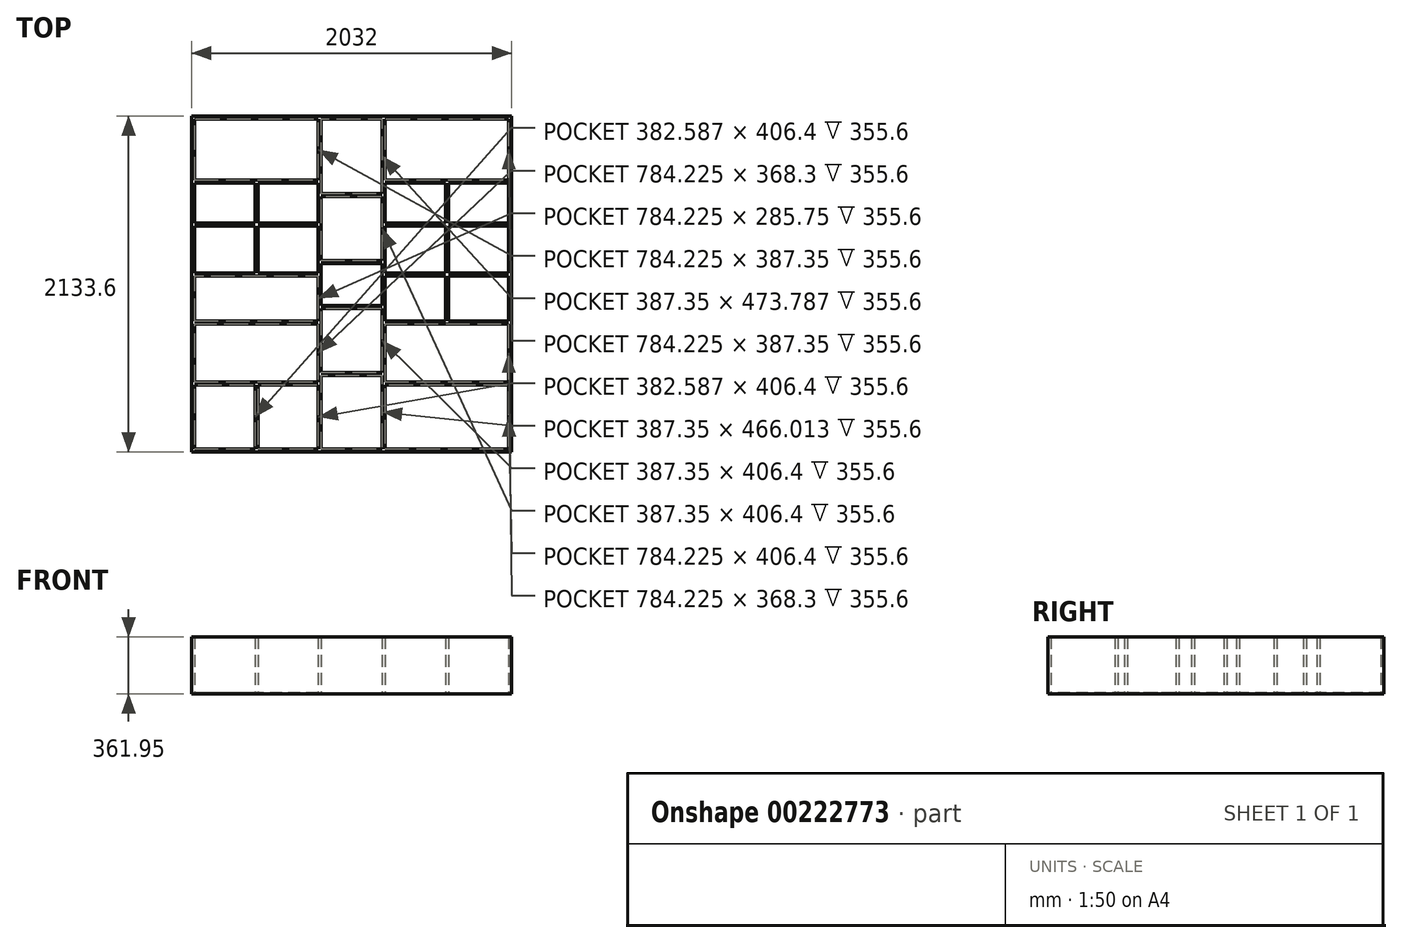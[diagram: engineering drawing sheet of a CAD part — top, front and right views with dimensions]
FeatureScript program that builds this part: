
annotation { "Feature Type Name" : "Feature", "Feature Type Description" : "" }
export const myFeature = defineFeature(function(context is Context, id is Id, definition is map)
    precondition{}
    {
        {
            var Q0;
            Q0=qCreatedBy(makeId("Top.planeOp"),FACE);
            var sketch = newSketch(context, id + "F0", { "sketchPlane" : qUnion([Q0])});
            skLineSegment(sketch, "E0.bottom", {"start": v(-1901.27, 1059.83) * mm, "end": v(130.73, 1059.83) * mm});
            skLineSegment(sketch, "E0.top", {"start": v(-1901.27, -1073.77) * mm, "end": v(130.73, -1073.77) * mm});
            skLineSegment(sketch, "E0.left", {"start": v(-1901.27, 1059.83) * mm, "end": v(-1901.27, -1073.77) * mm});
            skLineSegment(sketch, "E0.right", {"start": v(130.73, 1059.83) * mm, "end": v(130.73, -1073.77) * mm});
            skLineSegment(sketch, "E1", {"start": v(-1882.22, 1059.83) * mm, "end": v(-1882.22, -1073.77) * mm});
            skLineSegment(sketch, "E2", {"start": v(111.68, -1073.77) * mm, "end": v(111.68, 1059.83) * mm});
            skLineSegment(sketch, "E3", {"start": v(-682.07, 1059.83) * mm, "end": v(-682.07, 1132.47) * mm});
            skLineSegment(sketch, "E4", {"start": v(-1882.22, -1054.72) * mm, "end": v(111.68, -1054.72) * mm});
            skLineSegment(sketch, "E5", {"start": v(-1882.22, 1040.78) * mm, "end": v(111.68, 1040.78) * mm});
            skLineSegment(sketch, "E6", {"start": v(-672.55, 1040.78) * mm, "end": v(-672.55, -1054.72) * mm});
            skLineSegment(sketch, "E7", {"start": v(-691.6, 1040.78) * mm, "end": v(-691.6, -1054.72) * mm});
            skLineSegment(sketch, "E8.MirrorCS", {"start": v(-1078.95, 1040.78) * mm, "end": v(-1078.95, -1054.72) * mm});
            skLineSegment(sketch, "E9.MirrorCS", {"start": v(-1098, 1040.78) * mm, "end": v(-1098, -1054.72) * mm});
            skLineSegment(sketch, "E10", {"start": v(-672.55, 634.38) * mm, "end": v(111.68, 634.38) * mm});
            skLineSegment(sketch, "E11", {"start": v(-672.55, -648.32) * mm, "end": v(111.68, -648.32) * mm});
            skLineSegment(sketch, "E12", {"start": v(-672.55, -241.92) * mm, "end": v(111.68, -241.92) * mm});
            skLineSegment(sketch, "E13", {"start": v(-672.55, 62.88) * mm, "end": v(111.68, 62.88) * mm});
            skLineSegment(sketch, "E14", {"start": v(-672.55, 380.38) * mm, "end": v(111.68, 380.38) * mm});
            skLineSegment(sketch, "E15", {"start": v(-1078.95, -569.66) * mm, "end": v(-691.6, -569.66) * mm});
            skLineSegment(sketch, "E16", {"start": v(-1078.95, -163.26) * mm, "end": v(-691.6, -163.26) * mm});
            skLineSegment(sketch, "E17", {"start": v(-1078.95, 141.54) * mm, "end": v(-691.6, 141.54) * mm});
            skLineSegment(sketch, "E18", {"start": v(-1078.95, 547.94) * mm, "end": v(-691.6, 547.94) * mm});
            skLineSegment(sketch, "E19", {"start": v(-1098, -648.32) * mm, "end": v(-1882.22, -648.32) * mm});
            skLineSegment(sketch, "E20", {"start": v(-1098, -241.92) * mm, "end": v(-1882.22, -241.92) * mm});
            skLineSegment(sketch, "E21", {"start": v(-1098, 62.88) * mm, "end": v(-1882.22, 62.88) * mm});
            skLineSegment(sketch, "E22", {"start": v(-1098, 634.38) * mm, "end": v(-1882.22, 634.38) * mm});
            skLineSegment(sketch, "E23", {"start": v(-1882.22, 380.38) * mm, "end": v(-1098, 380.38) * mm});
            skLineSegment(sketch, "E24.0", {"start": v(-1098, 653.43) * mm, "end": v(-1882.22, 653.43) * mm});
            skLineSegment(sketch, "E25.0", {"start": v(-1098, -629.27) * mm, "end": v(-1882.22, -629.27) * mm});
            skLineSegment(sketch, "E26.0", {"start": v(-672.55, 653.43) * mm, "end": v(111.68, 653.43) * mm});
            skLineSegment(sketch, "E27.0", {"start": v(-672.55, -629.27) * mm, "end": v(111.68, -629.27) * mm});
            skLineSegment(sketch, "E28.0", {"start": v(-672.55, -260.97) * mm, "end": v(111.68, -260.97) * mm});
            skLineSegment(sketch, "E29.0", {"start": v(-1098, -260.97) * mm, "end": v(-1882.22, -260.97) * mm});
            skLineSegment(sketch, "E30.0", {"start": v(-1098, 43.83) * mm, "end": v(-1882.22, 43.83) * mm});
            skLineSegment(sketch, "E31.0", {"start": v(-672.55, 43.83) * mm, "end": v(111.68, 43.83) * mm});
            skLineSegment(sketch, "E32.0", {"start": v(-1882.22, 361.33) * mm, "end": v(-1098, 361.33) * mm});
            skLineSegment(sketch, "E33.0", {"start": v(-672.55, 361.33) * mm, "end": v(111.68, 361.33) * mm});
            skLineSegment(sketch, "E34.0", {"start": v(-1078.95, 567) * mm, "end": v(-691.6, 567) * mm});
            skLineSegment(sketch, "E35.0", {"start": v(-1078.95, -588.7) * mm, "end": v(-691.6, -588.7) * mm});
            skLineSegment(sketch, "E36.0", {"start": v(-1078.95, -144.2) * mm, "end": v(-691.6, -144.2) * mm});
            skLineSegment(sketch, "E37.0", {"start": v(-1078.95, 122.5) * mm, "end": v(-691.6, 122.5) * mm});
            skLineSegment(sketch, "E38.0", {"start": v(-1480.58, 62.88) * mm, "end": v(-1480.58, 634.38) * mm});
            skLineSegment(sketch, "E39.0", {"start": v(-1499.63, 62.88) * mm, "end": v(-1499.63, 634.38) * mm});
            skLineSegment(sketch, "E40.0", {"start": v(-289.96, -241.92) * mm, "end": v(-289.96, 634.38) * mm});
            skLineSegment(sketch, "E41.0", {"start": v(-270.9, -241.92) * mm, "end": v(-270.9, 634.38) * mm});
            skLineSegment(sketch, "E42.0", {"start": v(-1499.63, -648.32) * mm, "end": v(-1499.63, -1054.72) * mm});
            skLineSegment(sketch, "E43.0", {"start": v(-1480.58, -648.32) * mm, "end": v(-1480.58, -1054.72) * mm});
            skSolve(sketch);
        }
        {
            var Q0;
            {var subQ0=sQuery(id+"F0.wireOp",EDGE,"E12");var subQ1=sQuery(id+"F0.wireOp",EDGE,"E6");var subQ2=makeQuery(id+"F0.imprint","INTERSECT",VERTEX,{"derivedFrom":[subQ1,subQ0]});Q0=makeQuery(id+"F0.imprint","IMPRINT",FACE,{"disambiguationData":[TD([[makeQuery(id+"F0.imprint","IMPRINT",EDGE,{"disambiguationData":[TD([[subQ2,1.0]])],"derivedFrom":subQ1}),1.0]])]});}
            var Q1;
            {var subQ0=sQuery(id+"F0.wireOp",EDGE,"E15");Q1=makeQuery(id+"F0.imprint","IMPRINT",FACE,{"disambiguationData":[TD([[makeQuery(id+"F0.imprint","IMPRINT",EDGE,{"derivedFrom":subQ0}),1.0]])]});}
            var Q2;
            {var subQ0=sQuery(id+"F0.wireOp",EDGE,"E23");var subQ1=sQuery(id+"F0.wireOp",EDGE,"E9.MirrorCS");var subQ2=makeQuery(id+"F0.imprint","INTERSECT",VERTEX,{"derivedFrom":[subQ1,subQ0]});Q2=makeQuery(id+"F0.imprint","IMPRINT",FACE,{"disambiguationData":[TD([[makeQuery(id+"F0.imprint","IMPRINT",EDGE,{"disambiguationData":[TD([[subQ2,-1.0]])],"derivedFrom":subQ1}),-1.0]])]});}
            var Q3;
            {var subQ1=sQuery(id+"F0.wireOp",EDGE,"E1");var subQ5=sQuery(id+"F0.wireOp",EDGE,"E0.top");var subQ10=makeQuery(id+"F0.imprint","INTERSECT",VERTEX,{"derivedFrom":[subQ5,subQ1]});Q3=makeQuery(id+"F0.imprint","IMPRINT",FACE,{"disambiguationData":[TD([[makeQuery(id+"F0.imprint","IMPRINT",EDGE,{"disambiguationData":[TD([[subQ10,-1.0]])],"derivedFrom":subQ5}),1.0]])]});}
            var Q4;
            {var subQ0=sQuery(id+"F0.wireOp",EDGE,"E14");var subQ1=sQuery(id+"F0.wireOp",EDGE,"E2");var subQ2=makeQuery(id+"F0.imprint","INTERSECT",VERTEX,{"derivedFrom":[subQ1,subQ0]});Q4=makeQuery(id+"F0.imprint","IMPRINT",FACE,{"disambiguationData":[TD([[makeQuery(id+"F0.imprint","IMPRINT",EDGE,{"disambiguationData":[TD([[subQ2,1.0]])],"derivedFrom":subQ1}),1.0]])]});}
            var Q5;
            {var subQ0=sQuery(id+"F0.wireOp",EDGE,"E13");var subQ1=sQuery(id+"F0.wireOp",EDGE,"E2");var subQ2=makeQuery(id+"F0.imprint","INTERSECT",VERTEX,{"derivedFrom":[subQ1,subQ0]});Q5=makeQuery(id+"F0.imprint","IMPRINT",FACE,{"disambiguationData":[TD([[makeQuery(id+"F0.imprint","IMPRINT",EDGE,{"disambiguationData":[TD([[subQ2,-1.0]])],"derivedFrom":subQ1}),1.0]])]});}
            var Q6;
            {var subQ0=sQuery(id+"F0.wireOp",EDGE,"E10");var subQ1=sQuery(id+"F0.wireOp",EDGE,"E2");var subQ2=makeQuery(id+"F0.imprint","INTERSECT",VERTEX,{"derivedFrom":[subQ1,subQ0]});Q6=makeQuery(id+"F0.imprint","IMPRINT",FACE,{"disambiguationData":[TD([[makeQuery(id+"F0.imprint","IMPRINT",EDGE,{"disambiguationData":[TD([[subQ2,1.0]])],"derivedFrom":subQ1}),1.0]])]});}
            var Q7;
            {var subQ3=sQuery(id+"F0.wireOp",EDGE,"E43.0");Q7=makeQuery(id+"F0.imprint","IMPRINT",FACE,{"disambiguationData":[TD([[makeQuery(id+"F0.imprint","IMPRINT",EDGE,{"derivedFrom":subQ3}),1.0]])]});}
            var Q8;
            {var subQ0=sQuery(id+"F0.wireOp",EDGE,"E13");var subQ1=sQuery(id+"F0.wireOp",EDGE,"E6");var subQ2=makeQuery(id+"F0.imprint","INTERSECT",VERTEX,{"derivedFrom":[subQ1,subQ0]});Q8=makeQuery(id+"F0.imprint","IMPRINT",FACE,{"disambiguationData":[TD([[makeQuery(id+"F0.imprint","IMPRINT",EDGE,{"disambiguationData":[TD([[subQ2,-1.0]])],"derivedFrom":subQ1}),1.0]])]});}
            var Q9;
            {var subQ0=sQuery(id+"F0.wireOp",EDGE,"E14");var subQ1=sQuery(id+"F0.wireOp",EDGE,"E6");var subQ2=makeQuery(id+"F0.imprint","INTERSECT",VERTEX,{"derivedFrom":[subQ1,subQ0]});Q9=makeQuery(id+"F0.imprint","IMPRINT",FACE,{"disambiguationData":[TD([[makeQuery(id+"F0.imprint","IMPRINT",EDGE,{"disambiguationData":[TD([[subQ2,-1.0]])],"derivedFrom":subQ1}),1.0]])]});}
            var Q10;
            {var subQ0=sQuery(id+"F0.wireOp",EDGE,"E6");var subQ16=sQuery(id+"F0.wireOp",EDGE,"E4");var subQ17=makeQuery(id+"F0.imprint","INTERSECT",VERTEX,{"derivedFrom":[subQ16,subQ0]});Q10=makeQuery(id+"F0.imprint","IMPRINT",FACE,{"disambiguationData":[TD([[makeQuery(id+"F0.imprint","IMPRINT",EDGE,{"disambiguationData":[TD([[subQ17,1.0]])],"derivedFrom":subQ16}),1.0]])]});}
            var Q11;
            {var subQ0=sQuery(id+"F0.wireOp",EDGE,"E17");Q11=makeQuery(id+"F0.imprint","IMPRINT",FACE,{"disambiguationData":[TD([[makeQuery(id+"F0.imprint","IMPRINT",EDGE,{"derivedFrom":subQ0}),-1.0]])]});}
            var Q12;
            {var subQ7=sQuery(id+"F0.wireOp",EDGE,"E24.0");Q12=makeQuery(id+"F0.imprint","IMPRINT",FACE,{"disambiguationData":[TD([[makeQuery(id+"F0.imprint","IMPRINT",EDGE,{"derivedFrom":subQ7}),1.0]])]});}
            var Q13;
            {var subQ0=sQuery(id+"F0.wireOp",EDGE,"E16");Q13=makeQuery(id+"F0.imprint","IMPRINT",FACE,{"disambiguationData":[TD([[makeQuery(id+"F0.imprint","IMPRINT",EDGE,{"derivedFrom":subQ0}),1.0]])]});}
            var Q14;
            {var subQ1=sQuery(id+"F0.wireOp",EDGE,"E0.bottom");var subQ8=makeQuery(id+"F0.imprint","IMPRINT",VERTEX,{"derivedFrom":subQ1});Q14=makeQuery(id+"F0.imprint","IMPRINT",FACE,{"disambiguationData":[TD([[makeQuery(id+"F0.imprint","IMPRINT",EDGE,{"disambiguationData":[TD([[subQ8,1.0]])],"derivedFrom":subQ1}),-1.0]])]});}
            var Q15;
            {var subQ0=sQuery(id+"F0.wireOp",EDGE,"E22");var subQ1=sQuery(id+"F0.wireOp",EDGE,"E9.MirrorCS");var subQ2=makeQuery(id+"F0.imprint","INTERSECT",VERTEX,{"derivedFrom":[subQ1,subQ0]});Q15=makeQuery(id+"F0.imprint","IMPRINT",FACE,{"disambiguationData":[TD([[makeQuery(id+"F0.imprint","IMPRINT",EDGE,{"disambiguationData":[TD([[subQ2,-1.0]])],"derivedFrom":subQ1}),-1.0]])]});}
            var Q16;
            {var subQ5=sQuery(id+"F0.wireOp",EDGE,"E25.0");Q16=makeQuery(id+"F0.imprint","IMPRINT",FACE,{"disambiguationData":[TD([[makeQuery(id+"F0.imprint","IMPRINT",EDGE,{"derivedFrom":subQ5}),1.0]])]});}
            var Q17;
            {var subQ0=sQuery(id+"F0.wireOp",EDGE,"E8.MirrorCS");var subQ15=sQuery(id+"F0.wireOp",EDGE,"E4");var subQ16=makeQuery(id+"F0.imprint","INTERSECT",VERTEX,{"derivedFrom":[subQ15,subQ0]});Q17=makeQuery(id+"F0.imprint","IMPRINT",FACE,{"disambiguationData":[TD([[makeQuery(id+"F0.imprint","IMPRINT",EDGE,{"disambiguationData":[TD([[subQ16,1.0]])],"derivedFrom":subQ15}),1.0]])]});}
            var Q18;
            {var subQ0=sQuery(id+"F0.wireOp",EDGE,"E42.0");Q18=makeQuery(id+"F0.imprint","IMPRINT",FACE,{"disambiguationData":[TD([[makeQuery(id+"F0.imprint","IMPRINT",EDGE,{"derivedFrom":subQ0}),1.0]])]});}
            var Q19;
            {var subQ0=sQuery(id+"F0.wireOp",EDGE,"E40.0");var subQ1=sQuery(id+"F0.wireOp",EDGE,"E13");var subQ2=makeQuery(id+"F0.imprint","INTERSECT",VERTEX,{"derivedFrom":[subQ1,subQ0]});Q19=makeQuery(id+"F0.imprint","IMPRINT",FACE,{"disambiguationData":[TD([[makeQuery(id+"F0.imprint","IMPRINT",EDGE,{"disambiguationData":[TD([[subQ2,-1.0]])],"derivedFrom":subQ1}),1.0]])]});}
            var Q20;
            {var subQ0=sQuery(id+"F0.wireOp",EDGE,"E13");var subQ1=sQuery(id+"F0.wireOp",EDGE,"E6");var subQ2=makeQuery(id+"F0.imprint","INTERSECT",VERTEX,{"derivedFrom":[subQ1,subQ0]});Q20=makeQuery(id+"F0.imprint","IMPRINT",FACE,{"disambiguationData":[TD([[makeQuery(id+"F0.imprint","IMPRINT",EDGE,{"disambiguationData":[TD([[subQ2,1.0]])],"derivedFrom":subQ1}),1.0]])]});}
            var Q21;
            {var subQ0=sQuery(id+"F0.wireOp",EDGE,"E10");var subQ1=sQuery(id+"F0.wireOp",EDGE,"E6");var subQ2=makeQuery(id+"F0.imprint","INTERSECT",VERTEX,{"derivedFrom":[subQ1,subQ0]});Q21=makeQuery(id+"F0.imprint","IMPRINT",FACE,{"disambiguationData":[TD([[makeQuery(id+"F0.imprint","IMPRINT",EDGE,{"disambiguationData":[TD([[subQ2,-1.0]])],"derivedFrom":subQ1}),1.0]])]});}
            var Q22;
            {var subQ0=sQuery(id+"F0.wireOp",EDGE,"E13");var subQ1=sQuery(id+"F0.wireOp",EDGE,"E2");var subQ2=makeQuery(id+"F0.imprint","INTERSECT",VERTEX,{"derivedFrom":[subQ1,subQ0]});Q22=makeQuery(id+"F0.imprint","IMPRINT",FACE,{"disambiguationData":[TD([[makeQuery(id+"F0.imprint","IMPRINT",EDGE,{"disambiguationData":[TD([[subQ2,1.0]])],"derivedFrom":subQ1}),1.0]])]});}
            var Q23;
            {var subQ0=sQuery(id+"F0.wireOp",EDGE,"E21");var subQ1=sQuery(id+"F0.wireOp",EDGE,"E9.MirrorCS");var subQ2=makeQuery(id+"F0.imprint","INTERSECT",VERTEX,{"derivedFrom":[subQ1,subQ0]});Q23=makeQuery(id+"F0.imprint","IMPRINT",FACE,{"disambiguationData":[TD([[makeQuery(id+"F0.imprint","IMPRINT",EDGE,{"disambiguationData":[TD([[subQ2,1.0]])],"derivedFrom":subQ1}),-1.0]])]});}
            var Q24;
            {var subQ0=sQuery(id+"F0.wireOp",EDGE,"E12");var subQ1=sQuery(id+"F0.wireOp",EDGE,"E2");var subQ2=makeQuery(id+"F0.imprint","INTERSECT",VERTEX,{"derivedFrom":[subQ1,subQ0]});Q24=makeQuery(id+"F0.imprint","IMPRINT",FACE,{"disambiguationData":[TD([[makeQuery(id+"F0.imprint","IMPRINT",EDGE,{"disambiguationData":[TD([[subQ2,-1.0]])],"derivedFrom":subQ1}),1.0]])]});}
            var Q25;
            {var subQ3=sQuery(id+"F0.wireOp",EDGE,"E11");Q25=makeQuery(id+"F0.imprint","IMPRINT",FACE,{"disambiguationData":[TD([[makeQuery(id+"F0.imprint","IMPRINT",EDGE,{"derivedFrom":subQ3}),-1.0]])]});}
            var Q26;
            {var subQ0=sQuery(id+"F0.wireOp",EDGE,"E11");Q26=makeQuery(id+"F0.imprint","IMPRINT",FACE,{"disambiguationData":[TD([[makeQuery(id+"F0.imprint","IMPRINT",EDGE,{"derivedFrom":subQ0}),1.0]])]});}
            var Q27;
            {var subQ0=sQuery(id+"F0.wireOp",EDGE,"E27.0");Q27=makeQuery(id+"F0.imprint","IMPRINT",FACE,{"disambiguationData":[TD([[makeQuery(id+"F0.imprint","IMPRINT",EDGE,{"derivedFrom":subQ0}),1.0]])]});}
            var Q28;
            {var subQ5=sQuery(id+"F0.wireOp",EDGE,"E42.0");Q28=makeQuery(id+"F0.imprint","IMPRINT",FACE,{"disambiguationData":[TD([[makeQuery(id+"F0.imprint","IMPRINT",EDGE,{"derivedFrom":subQ5}),-1.0]])]});}
            var Q29;
            {var subQ0=sQuery(id+"F0.wireOp",EDGE,"E25.0");Q29=makeQuery(id+"F0.imprint","IMPRINT",FACE,{"disambiguationData":[TD([[makeQuery(id+"F0.imprint","IMPRINT",EDGE,{"derivedFrom":subQ0}),-1.0]])]});}
            var Q30;
            {var subQ0=sQuery(id+"F0.wireOp",EDGE,"E17");Q30=makeQuery(id+"F0.imprint","IMPRINT",FACE,{"disambiguationData":[TD([[makeQuery(id+"F0.imprint","IMPRINT",EDGE,{"derivedFrom":subQ0}),1.0]])]});}
            var Q31;
            {var subQ0=sQuery(id+"F0.wireOp",EDGE,"E20");Q31=makeQuery(id+"F0.imprint","IMPRINT",FACE,{"disambiguationData":[TD([[makeQuery(id+"F0.imprint","IMPRINT",EDGE,{"derivedFrom":subQ0}),1.0]])]});}
            var Q32;
            {var subQ0=sQuery(id+"F0.wireOp",EDGE,"E20");Q32=makeQuery(id+"F0.imprint","IMPRINT",FACE,{"disambiguationData":[TD([[makeQuery(id+"F0.imprint","IMPRINT",EDGE,{"derivedFrom":subQ0}),-1.0]])]});}
            var Q33;
            {var subQ0=sQuery(id+"F0.wireOp",EDGE,"E21");var subQ1=sQuery(id+"F0.wireOp",EDGE,"E1");var subQ2=makeQuery(id+"F0.imprint","INTERSECT",VERTEX,{"derivedFrom":[subQ1,subQ0]});Q33=makeQuery(id+"F0.imprint","IMPRINT",FACE,{"disambiguationData":[TD([[makeQuery(id+"F0.imprint","IMPRINT",EDGE,{"disambiguationData":[TD([[subQ2,1.0]])],"derivedFrom":subQ1}),1.0]])]});}
            var Q34;
            {var subQ0=sQuery(id+"F0.wireOp",EDGE,"E23");var subQ1=sQuery(id+"F0.wireOp",EDGE,"E1");var subQ2=makeQuery(id+"F0.imprint","INTERSECT",VERTEX,{"derivedFrom":[subQ1,subQ0]});Q34=makeQuery(id+"F0.imprint","IMPRINT",FACE,{"disambiguationData":[TD([[makeQuery(id+"F0.imprint","IMPRINT",EDGE,{"disambiguationData":[TD([[subQ2,-1.0]])],"derivedFrom":subQ1}),1.0]])]});}
            var Q35;
            {var subQ0=sQuery(id+"F0.wireOp",EDGE,"E22");var subQ1=sQuery(id+"F0.wireOp",EDGE,"E1");var subQ2=makeQuery(id+"F0.imprint","INTERSECT",VERTEX,{"derivedFrom":[subQ1,subQ0]});Q35=makeQuery(id+"F0.imprint","IMPRINT",FACE,{"disambiguationData":[TD([[makeQuery(id+"F0.imprint","IMPRINT",EDGE,{"disambiguationData":[TD([[subQ2,-1.0]])],"derivedFrom":subQ1}),1.0]])]});}
            var Q36;
            {var subQ13=sQuery(id+"F0.wireOp",EDGE,"E0.left");Q36=makeQuery(id+"F0.imprint","IMPRINT",FACE,{"disambiguationData":[TD([[makeQuery(id+"F0.imprint","IMPRINT",EDGE,{"derivedFrom":subQ13}),1.0]])]});}
            var Q37;
            {var subQ0=sQuery(id+"F0.wireOp",EDGE,"E36.0");Q37=makeQuery(id+"F0.imprint","IMPRINT",FACE,{"disambiguationData":[TD([[makeQuery(id+"F0.imprint","IMPRINT",EDGE,{"derivedFrom":subQ0}),1.0]])]});}
            var Q38;
            {var subQ5=sQuery(id+"F0.wireOp",EDGE,"E30.0");Q38=makeQuery(id+"F0.imprint","IMPRINT",FACE,{"disambiguationData":[TD([[makeQuery(id+"F0.imprint","IMPRINT",EDGE,{"derivedFrom":subQ5}),-1.0]])]});}
            var Q39;
            {var subQ13=sQuery(id+"F0.wireOp",EDGE,"E0.right");Q39=makeQuery(id+"F0.imprint","IMPRINT",FACE,{"disambiguationData":[TD([[makeQuery(id+"F0.imprint","IMPRINT",EDGE,{"derivedFrom":subQ13}),-1.0]])]});}
            var Q40;
            {var subQ3=sQuery(id+"F0.wireOp",EDGE,"E24.0");Q40=makeQuery(id+"F0.imprint","IMPRINT",FACE,{"disambiguationData":[TD([[makeQuery(id+"F0.imprint","IMPRINT",EDGE,{"derivedFrom":subQ3}),-1.0]])]});}
            var Q41;
            {var subQ0=sQuery(id+"F0.wireOp",EDGE,"E15");Q41=makeQuery(id+"F0.imprint","IMPRINT",FACE,{"disambiguationData":[TD([[makeQuery(id+"F0.imprint","IMPRINT",EDGE,{"derivedFrom":subQ0}),-1.0]])]});}
            var Q42;
            {var subQ5=sQuery(id+"F0.wireOp",EDGE,"E26.0");Q42=makeQuery(id+"F0.imprint","IMPRINT",FACE,{"disambiguationData":[TD([[makeQuery(id+"F0.imprint","IMPRINT",EDGE,{"derivedFrom":subQ5}),-1.0]])]});}
            var Q43;
            {var subQ5=sQuery(id+"F0.wireOp",EDGE,"E34.0");Q43=makeQuery(id+"F0.imprint","IMPRINT",FACE,{"disambiguationData":[TD([[makeQuery(id+"F0.imprint","IMPRINT",EDGE,{"derivedFrom":subQ5}),1.0]])]});}
            var Q44;
            {var subQ5=sQuery(id+"F0.wireOp",EDGE,"E35.0");Q44=makeQuery(id+"F0.imprint","IMPRINT",FACE,{"disambiguationData":[TD([[makeQuery(id+"F0.imprint","IMPRINT",EDGE,{"derivedFrom":subQ5}),-1.0]])]});}
            var Q45;
            {var subQ3=sQuery(id+"F0.wireOp",EDGE,"E26.0");Q45=makeQuery(id+"F0.imprint","IMPRINT",FACE,{"disambiguationData":[TD([[makeQuery(id+"F0.imprint","IMPRINT",EDGE,{"derivedFrom":subQ3}),1.0]])]});}
            var Q46;
            {var subQ0=sQuery(id+"F0.wireOp",EDGE,"E18");Q46=makeQuery(id+"F0.imprint","IMPRINT",FACE,{"disambiguationData":[TD([[makeQuery(id+"F0.imprint","IMPRINT",EDGE,{"derivedFrom":subQ0}),1.0]])]});}
            var Q47;
            {var subQ5=sQuery(id+"F0.wireOp",EDGE,"E28.0");Q47=makeQuery(id+"F0.imprint","IMPRINT",FACE,{"disambiguationData":[TD([[makeQuery(id+"F0.imprint","IMPRINT",EDGE,{"derivedFrom":subQ5}),1.0]])]});}
            var Q48;
            {var subQ0=sQuery(id+"F0.wireOp",EDGE,"E38.0");var subQ1=sQuery(id+"F0.wireOp",EDGE,"E21");var subQ2=makeQuery(id+"F0.imprint","INTERSECT",VERTEX,{"derivedFrom":[subQ1,subQ0]});Q48=makeQuery(id+"F0.imprint","IMPRINT",FACE,{"disambiguationData":[TD([[makeQuery(id+"F0.imprint","IMPRINT",EDGE,{"disambiguationData":[TD([[subQ2,-1.0]])],"derivedFrom":subQ1}),-1.0]])]});}
            var Q49;
            {var subQ0=sQuery(id+"F0.wireOp",EDGE,"E40.0");var subQ1=sQuery(id+"F0.wireOp",EDGE,"E14");var subQ2=makeQuery(id+"F0.imprint","INTERSECT",VERTEX,{"derivedFrom":[subQ1,subQ0]});Q49=makeQuery(id+"F0.imprint","IMPRINT",FACE,{"disambiguationData":[TD([[makeQuery(id+"F0.imprint","IMPRINT",EDGE,{"disambiguationData":[TD([[subQ2,-1.0]])],"derivedFrom":subQ1}),-1.0]])]});}
            var Q50;
            {var subQ0=sQuery(id+"F0.wireOp",EDGE,"E40.0");var subQ1=sQuery(id+"F0.wireOp",EDGE,"E13");var subQ2=makeQuery(id+"F0.imprint","INTERSECT",VERTEX,{"derivedFrom":[subQ1,subQ0]});Q50=makeQuery(id+"F0.imprint","IMPRINT",FACE,{"disambiguationData":[TD([[makeQuery(id+"F0.imprint","IMPRINT",EDGE,{"disambiguationData":[TD([[subQ2,-1.0]])],"derivedFrom":subQ1}),-1.0]])]});}
            var Q51;
            {var subQ0=sQuery(id+"F0.wireOp",EDGE,"E40.0");var subQ1=sQuery(id+"F0.wireOp",EDGE,"E12");var subQ2=makeQuery(id+"F0.imprint","INTERSECT",VERTEX,{"derivedFrom":[subQ1,subQ0]});Q51=makeQuery(id+"F0.imprint","IMPRINT",FACE,{"disambiguationData":[TD([[makeQuery(id+"F0.imprint","IMPRINT",EDGE,{"disambiguationData":[TD([[subQ2,-1.0]])],"derivedFrom":subQ1}),1.0]])]});}
            var Q52;
            {var subQ0=sQuery(id+"F0.wireOp",EDGE,"E39.0");var subQ1=sQuery(id+"F0.wireOp",EDGE,"E23");var subQ2=makeQuery(id+"F0.imprint","INTERSECT",VERTEX,{"derivedFrom":[subQ1,subQ0]});Q52=makeQuery(id+"F0.imprint","IMPRINT",FACE,{"disambiguationData":[TD([[makeQuery(id+"F0.imprint","IMPRINT",EDGE,{"disambiguationData":[TD([[subQ2,-1.0]])],"derivedFrom":subQ1}),-1.0]])]});}
            var Q53;
            {var subQ0=sQuery(id+"F0.wireOp",EDGE,"E40.0");var subQ1=sQuery(id+"F0.wireOp",EDGE,"E10");var subQ2=makeQuery(id+"F0.imprint","INTERSECT",VERTEX,{"derivedFrom":[subQ1,subQ0]});Q53=makeQuery(id+"F0.imprint","IMPRINT",FACE,{"disambiguationData":[TD([[makeQuery(id+"F0.imprint","IMPRINT",EDGE,{"disambiguationData":[TD([[subQ2,-1.0]])],"derivedFrom":subQ1}),-1.0]])]});}
            var Q54;
            {var subQ0=sQuery(id+"F0.wireOp",EDGE,"E38.0");var subQ1=sQuery(id+"F0.wireOp",EDGE,"E22");var subQ2=makeQuery(id+"F0.imprint","INTERSECT",VERTEX,{"derivedFrom":[subQ1,subQ0]});Q54=makeQuery(id+"F0.imprint","IMPRINT",FACE,{"disambiguationData":[TD([[makeQuery(id+"F0.imprint","IMPRINT",EDGE,{"disambiguationData":[TD([[subQ2,-1.0]])],"derivedFrom":subQ1}),1.0]])]});}
            extrude(context, id + "F1", {"entities" : qUnion([Q0, Q1, Q2, Q3, Q4, Q5, Q6, Q7, Q8, Q9, Q10, Q11, Q12, Q13, Q14, Q15, Q16, Q17, Q18, Q19, Q20, Q21, Q22, Q23, Q24, Q25, Q26, Q27, Q28, Q29, Q30, Q31, Q32, Q33, Q34, Q35, Q36, Q37, Q38, Q39, Q40, Q41, Q42, Q43, Q44, Q45, Q46, Q47, Q48, Q49, Q50, Q51, Q52, Q53, Q54]), "oppositeDirection" : true, "depth" : 6.35 * mm});
        }
        {
            var Q0;
            {var subQ13=sQuery(id+"F0.wireOp",EDGE,"E0.left");Q0=makeQuery(id+"F0.imprint","IMPRINT",FACE,{"disambiguationData":[TD([[makeQuery(id+"F0.imprint","IMPRINT",EDGE,{"derivedFrom":subQ13}),1.0]])]});}
            var Q1;
            {var subQ1=sQuery(id+"F0.wireOp",EDGE,"E0.bottom");var subQ8=makeQuery(id+"F0.imprint","IMPRINT",VERTEX,{"derivedFrom":subQ1});Q1=makeQuery(id+"F0.imprint","IMPRINT",FACE,{"disambiguationData":[TD([[makeQuery(id+"F0.imprint","IMPRINT",EDGE,{"disambiguationData":[TD([[subQ8,1.0]])],"derivedFrom":subQ1}),-1.0]])]});}
            var Q2;
            {var subQ7=sQuery(id+"F0.wireOp",EDGE,"E24.0");Q2=makeQuery(id+"F0.imprint","IMPRINT",FACE,{"disambiguationData":[TD([[makeQuery(id+"F0.imprint","IMPRINT",EDGE,{"derivedFrom":subQ7}),1.0]])]});}
            var Q3;
            {var subQ0=sQuery(id+"F0.wireOp",EDGE,"E38.0");var subQ1=sQuery(id+"F0.wireOp",EDGE,"E22");var subQ2=makeQuery(id+"F0.imprint","INTERSECT",VERTEX,{"derivedFrom":[subQ1,subQ0]});Q3=makeQuery(id+"F0.imprint","IMPRINT",FACE,{"disambiguationData":[TD([[makeQuery(id+"F0.imprint","IMPRINT",EDGE,{"disambiguationData":[TD([[subQ2,-1.0]])],"derivedFrom":subQ1}),1.0]])]});}
            var Q4;
            {var subQ0=sQuery(id+"F0.wireOp",EDGE,"E23");var subQ1=sQuery(id+"F0.wireOp",EDGE,"E1");var subQ2=makeQuery(id+"F0.imprint","INTERSECT",VERTEX,{"derivedFrom":[subQ1,subQ0]});Q4=makeQuery(id+"F0.imprint","IMPRINT",FACE,{"disambiguationData":[TD([[makeQuery(id+"F0.imprint","IMPRINT",EDGE,{"disambiguationData":[TD([[subQ2,-1.0]])],"derivedFrom":subQ1}),1.0]])]});}
            var Q5;
            {var subQ0=sQuery(id+"F0.wireOp",EDGE,"E39.0");var subQ1=sQuery(id+"F0.wireOp",EDGE,"E23");var subQ2=makeQuery(id+"F0.imprint","INTERSECT",VERTEX,{"derivedFrom":[subQ1,subQ0]});Q5=makeQuery(id+"F0.imprint","IMPRINT",FACE,{"disambiguationData":[TD([[makeQuery(id+"F0.imprint","IMPRINT",EDGE,{"disambiguationData":[TD([[subQ2,-1.0]])],"derivedFrom":subQ1}),-1.0]])]});}
            var Q6;
            {var subQ0=sQuery(id+"F0.wireOp",EDGE,"E23");var subQ1=sQuery(id+"F0.wireOp",EDGE,"E9.MirrorCS");var subQ2=makeQuery(id+"F0.imprint","INTERSECT",VERTEX,{"derivedFrom":[subQ1,subQ0]});Q6=makeQuery(id+"F0.imprint","IMPRINT",FACE,{"disambiguationData":[TD([[makeQuery(id+"F0.imprint","IMPRINT",EDGE,{"disambiguationData":[TD([[subQ2,-1.0]])],"derivedFrom":subQ1}),-1.0]])]});}
            var Q7;
            {var subQ0=sQuery(id+"F0.wireOp",EDGE,"E38.0");var subQ1=sQuery(id+"F0.wireOp",EDGE,"E21");var subQ2=makeQuery(id+"F0.imprint","INTERSECT",VERTEX,{"derivedFrom":[subQ1,subQ0]});Q7=makeQuery(id+"F0.imprint","IMPRINT",FACE,{"disambiguationData":[TD([[makeQuery(id+"F0.imprint","IMPRINT",EDGE,{"disambiguationData":[TD([[subQ2,-1.0]])],"derivedFrom":subQ1}),-1.0]])]});}
            var Q8;
            {var subQ5=sQuery(id+"F0.wireOp",EDGE,"E30.0");Q8=makeQuery(id+"F0.imprint","IMPRINT",FACE,{"disambiguationData":[TD([[makeQuery(id+"F0.imprint","IMPRINT",EDGE,{"derivedFrom":subQ5}),-1.0]])]});}
            var Q9;
            {var subQ0=sQuery(id+"F0.wireOp",EDGE,"E20");Q9=makeQuery(id+"F0.imprint","IMPRINT",FACE,{"disambiguationData":[TD([[makeQuery(id+"F0.imprint","IMPRINT",EDGE,{"derivedFrom":subQ0}),1.0]])]});}
            var Q10;
            {var subQ5=sQuery(id+"F0.wireOp",EDGE,"E25.0");Q10=makeQuery(id+"F0.imprint","IMPRINT",FACE,{"disambiguationData":[TD([[makeQuery(id+"F0.imprint","IMPRINT",EDGE,{"derivedFrom":subQ5}),1.0]])]});}
            var Q11;
            {var subQ0=sQuery(id+"F0.wireOp",EDGE,"E42.0");Q11=makeQuery(id+"F0.imprint","IMPRINT",FACE,{"disambiguationData":[TD([[makeQuery(id+"F0.imprint","IMPRINT",EDGE,{"derivedFrom":subQ0}),1.0]])]});}
            var Q12;
            {var subQ0=sQuery(id+"F0.wireOp",EDGE,"E8.MirrorCS");var subQ15=sQuery(id+"F0.wireOp",EDGE,"E4");var subQ16=makeQuery(id+"F0.imprint","INTERSECT",VERTEX,{"derivedFrom":[subQ15,subQ0]});Q12=makeQuery(id+"F0.imprint","IMPRINT",FACE,{"disambiguationData":[TD([[makeQuery(id+"F0.imprint","IMPRINT",EDGE,{"disambiguationData":[TD([[subQ16,1.0]])],"derivedFrom":subQ15}),1.0]])]});}
            var Q13;
            {var subQ1=sQuery(id+"F0.wireOp",EDGE,"E1");var subQ5=sQuery(id+"F0.wireOp",EDGE,"E0.top");var subQ10=makeQuery(id+"F0.imprint","INTERSECT",VERTEX,{"derivedFrom":[subQ5,subQ1]});Q13=makeQuery(id+"F0.imprint","IMPRINT",FACE,{"disambiguationData":[TD([[makeQuery(id+"F0.imprint","IMPRINT",EDGE,{"disambiguationData":[TD([[subQ10,-1.0]])],"derivedFrom":subQ5}),1.0]])]});}
            var Q14;
            {var subQ0=sQuery(id+"F0.wireOp",EDGE,"E18");Q14=makeQuery(id+"F0.imprint","IMPRINT",FACE,{"disambiguationData":[TD([[makeQuery(id+"F0.imprint","IMPRINT",EDGE,{"derivedFrom":subQ0}),1.0]])]});}
            var Q15;
            {var subQ0=sQuery(id+"F0.wireOp",EDGE,"E17");Q15=makeQuery(id+"F0.imprint","IMPRINT",FACE,{"disambiguationData":[TD([[makeQuery(id+"F0.imprint","IMPRINT",EDGE,{"derivedFrom":subQ0}),-1.0]])]});}
            var Q16;
            {var subQ0=sQuery(id+"F0.wireOp",EDGE,"E16");Q16=makeQuery(id+"F0.imprint","IMPRINT",FACE,{"disambiguationData":[TD([[makeQuery(id+"F0.imprint","IMPRINT",EDGE,{"derivedFrom":subQ0}),1.0]])]});}
            var Q17;
            {var subQ0=sQuery(id+"F0.wireOp",EDGE,"E15");Q17=makeQuery(id+"F0.imprint","IMPRINT",FACE,{"disambiguationData":[TD([[makeQuery(id+"F0.imprint","IMPRINT",EDGE,{"derivedFrom":subQ0}),-1.0]])]});}
            var Q18;
            {var subQ0=sQuery(id+"F0.wireOp",EDGE,"E6");var subQ16=sQuery(id+"F0.wireOp",EDGE,"E4");var subQ17=makeQuery(id+"F0.imprint","INTERSECT",VERTEX,{"derivedFrom":[subQ16,subQ0]});Q18=makeQuery(id+"F0.imprint","IMPRINT",FACE,{"disambiguationData":[TD([[makeQuery(id+"F0.imprint","IMPRINT",EDGE,{"disambiguationData":[TD([[subQ17,1.0]])],"derivedFrom":subQ16}),1.0]])]});}
            var Q19;
            {var subQ5=sQuery(id+"F0.wireOp",EDGE,"E26.0");Q19=makeQuery(id+"F0.imprint","IMPRINT",FACE,{"disambiguationData":[TD([[makeQuery(id+"F0.imprint","IMPRINT",EDGE,{"derivedFrom":subQ5}),-1.0]])]});}
            var Q20;
            {var subQ0=sQuery(id+"F0.wireOp",EDGE,"E40.0");var subQ1=sQuery(id+"F0.wireOp",EDGE,"E10");var subQ2=makeQuery(id+"F0.imprint","INTERSECT",VERTEX,{"derivedFrom":[subQ1,subQ0]});Q20=makeQuery(id+"F0.imprint","IMPRINT",FACE,{"disambiguationData":[TD([[makeQuery(id+"F0.imprint","IMPRINT",EDGE,{"disambiguationData":[TD([[subQ2,-1.0]])],"derivedFrom":subQ1}),-1.0]])]});}
            var Q21;
            {var subQ0=sQuery(id+"F0.wireOp",EDGE,"E14");var subQ1=sQuery(id+"F0.wireOp",EDGE,"E6");var subQ2=makeQuery(id+"F0.imprint","INTERSECT",VERTEX,{"derivedFrom":[subQ1,subQ0]});Q21=makeQuery(id+"F0.imprint","IMPRINT",FACE,{"disambiguationData":[TD([[makeQuery(id+"F0.imprint","IMPRINT",EDGE,{"disambiguationData":[TD([[subQ2,-1.0]])],"derivedFrom":subQ1}),1.0]])]});}
            var Q22;
            {var subQ0=sQuery(id+"F0.wireOp",EDGE,"E40.0");var subQ1=sQuery(id+"F0.wireOp",EDGE,"E14");var subQ2=makeQuery(id+"F0.imprint","INTERSECT",VERTEX,{"derivedFrom":[subQ1,subQ0]});Q22=makeQuery(id+"F0.imprint","IMPRINT",FACE,{"disambiguationData":[TD([[makeQuery(id+"F0.imprint","IMPRINT",EDGE,{"disambiguationData":[TD([[subQ2,-1.0]])],"derivedFrom":subQ1}),-1.0]])]});}
            var Q23;
            {var subQ0=sQuery(id+"F0.wireOp",EDGE,"E14");var subQ1=sQuery(id+"F0.wireOp",EDGE,"E2");var subQ2=makeQuery(id+"F0.imprint","INTERSECT",VERTEX,{"derivedFrom":[subQ1,subQ0]});Q23=makeQuery(id+"F0.imprint","IMPRINT",FACE,{"disambiguationData":[TD([[makeQuery(id+"F0.imprint","IMPRINT",EDGE,{"disambiguationData":[TD([[subQ2,1.0]])],"derivedFrom":subQ1}),1.0]])]});}
            var Q24;
            {var subQ0=sQuery(id+"F0.wireOp",EDGE,"E40.0");var subQ1=sQuery(id+"F0.wireOp",EDGE,"E13");var subQ2=makeQuery(id+"F0.imprint","INTERSECT",VERTEX,{"derivedFrom":[subQ1,subQ0]});Q24=makeQuery(id+"F0.imprint","IMPRINT",FACE,{"disambiguationData":[TD([[makeQuery(id+"F0.imprint","IMPRINT",EDGE,{"disambiguationData":[TD([[subQ2,-1.0]])],"derivedFrom":subQ1}),1.0]])]});}
            var Q25;
            {var subQ0=sQuery(id+"F0.wireOp",EDGE,"E40.0");var subQ1=sQuery(id+"F0.wireOp",EDGE,"E13");var subQ2=makeQuery(id+"F0.imprint","INTERSECT",VERTEX,{"derivedFrom":[subQ1,subQ0]});Q25=makeQuery(id+"F0.imprint","IMPRINT",FACE,{"disambiguationData":[TD([[makeQuery(id+"F0.imprint","IMPRINT",EDGE,{"disambiguationData":[TD([[subQ2,-1.0]])],"derivedFrom":subQ1}),-1.0]])]});}
            var Q26;
            {var subQ0=sQuery(id+"F0.wireOp",EDGE,"E13");var subQ1=sQuery(id+"F0.wireOp",EDGE,"E6");var subQ2=makeQuery(id+"F0.imprint","INTERSECT",VERTEX,{"derivedFrom":[subQ1,subQ0]});Q26=makeQuery(id+"F0.imprint","IMPRINT",FACE,{"disambiguationData":[TD([[makeQuery(id+"F0.imprint","IMPRINT",EDGE,{"disambiguationData":[TD([[subQ2,-1.0]])],"derivedFrom":subQ1}),1.0]])]});}
            var Q27;
            {var subQ0=sQuery(id+"F0.wireOp",EDGE,"E13");var subQ1=sQuery(id+"F0.wireOp",EDGE,"E2");var subQ2=makeQuery(id+"F0.imprint","INTERSECT",VERTEX,{"derivedFrom":[subQ1,subQ0]});Q27=makeQuery(id+"F0.imprint","IMPRINT",FACE,{"disambiguationData":[TD([[makeQuery(id+"F0.imprint","IMPRINT",EDGE,{"disambiguationData":[TD([[subQ2,1.0]])],"derivedFrom":subQ1}),1.0]])]});}
            var Q28;
            {var subQ0=sQuery(id+"F0.wireOp",EDGE,"E40.0");var subQ1=sQuery(id+"F0.wireOp",EDGE,"E12");var subQ2=makeQuery(id+"F0.imprint","INTERSECT",VERTEX,{"derivedFrom":[subQ1,subQ0]});Q28=makeQuery(id+"F0.imprint","IMPRINT",FACE,{"disambiguationData":[TD([[makeQuery(id+"F0.imprint","IMPRINT",EDGE,{"disambiguationData":[TD([[subQ2,-1.0]])],"derivedFrom":subQ1}),1.0]])]});}
            var Q29;
            {var subQ5=sQuery(id+"F0.wireOp",EDGE,"E28.0");Q29=makeQuery(id+"F0.imprint","IMPRINT",FACE,{"disambiguationData":[TD([[makeQuery(id+"F0.imprint","IMPRINT",EDGE,{"derivedFrom":subQ5}),1.0]])]});}
            var Q30;
            {var subQ0=sQuery(id+"F0.wireOp",EDGE,"E11");Q30=makeQuery(id+"F0.imprint","IMPRINT",FACE,{"disambiguationData":[TD([[makeQuery(id+"F0.imprint","IMPRINT",EDGE,{"derivedFrom":subQ0}),1.0]])]});}
            var Q31;
            {var subQ13=sQuery(id+"F0.wireOp",EDGE,"E0.right");Q31=makeQuery(id+"F0.imprint","IMPRINT",FACE,{"disambiguationData":[TD([[makeQuery(id+"F0.imprint","IMPRINT",EDGE,{"derivedFrom":subQ13}),-1.0]])]});}
            extrude(context, id + "F2", {"entities" : qUnion([Q0, Q1, Q2, Q3, Q4, Q5, Q6, Q7, Q8, Q9, Q10, Q11, Q12, Q13, Q14, Q15, Q16, Q17, Q18, Q19, Q20, Q21, Q22, Q23, Q24, Q25, Q26, Q27, Q28, Q29, Q30, Q31]), "operationType" : NewBodyOperationType.ADD, "depth" : 355.6 * mm});
        }
    });
